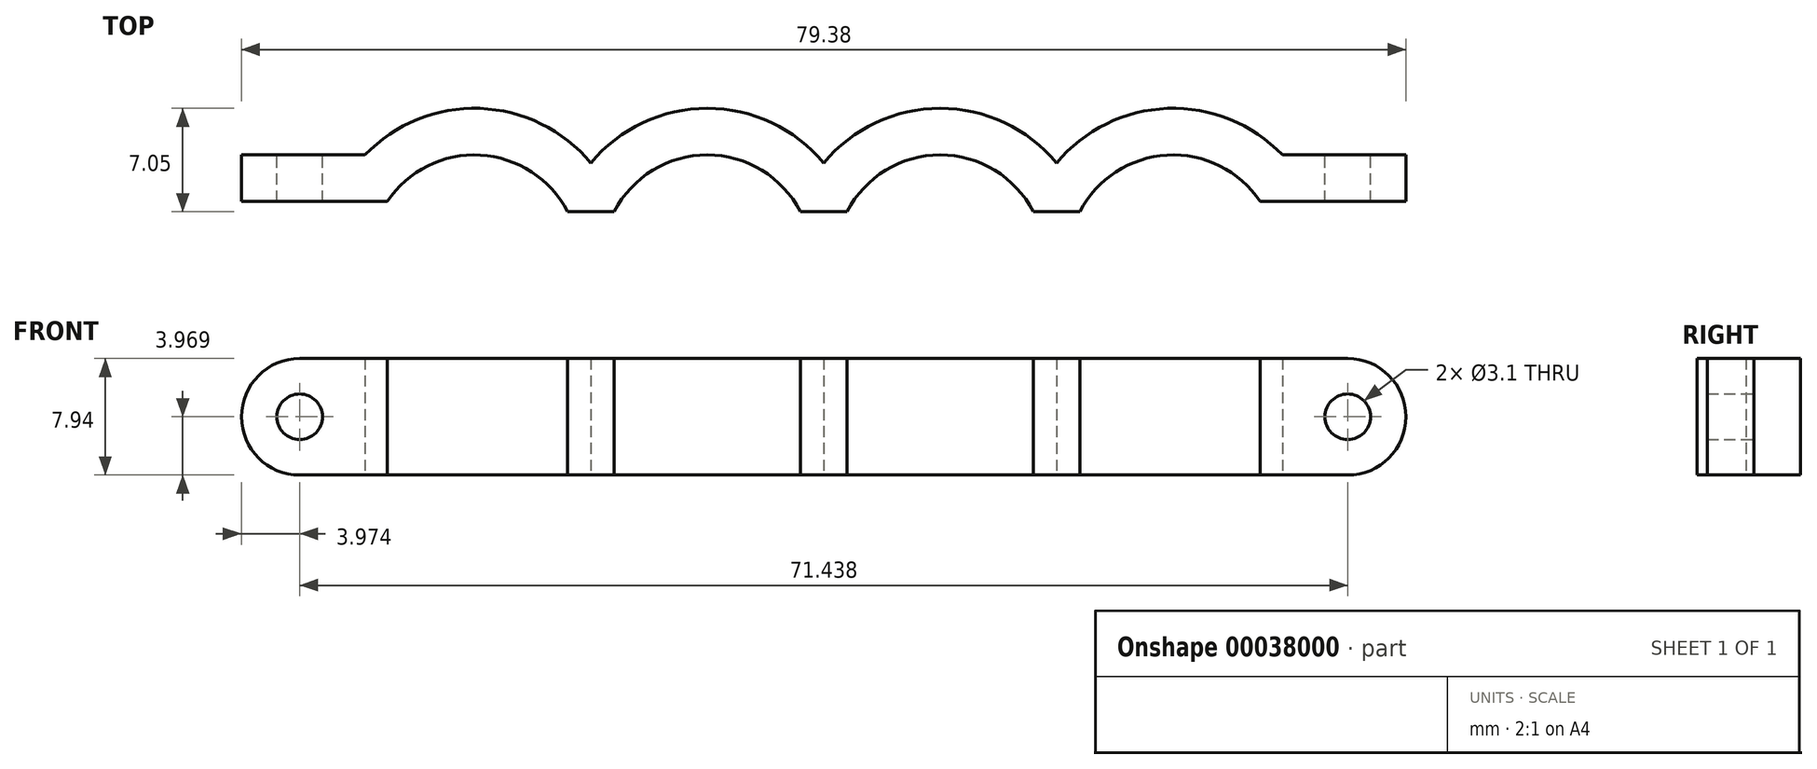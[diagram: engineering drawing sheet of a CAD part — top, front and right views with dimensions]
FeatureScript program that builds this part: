
annotation { "Feature Type Name" : "Feature", "Feature Type Description" : "" }
export const myFeature = defineFeature(function(context is Context, id is Id, definition is map)
    precondition{}
    {
        {
            var Q0;
            Q0=qCreatedBy(makeId("Top.planeOp"),FACE);
            var sketch = newSketch(context, id + "F0", { "sketchPlane" : qUnion([Q0])});
            skLineSegment(sketch, "E0.bottom", {"start": v(0, 0) * mm, "end": v(-9.94, 0) * mm});
            skLineSegment(sketch, "E0.right", {"start": v(-9.94, 0) * mm, "end": v(-9.94, 3.18) * mm});
            skArc(sketch, "E1", {"start": v(12.29, -0.7) * mm, "mid": v(6.34, 3.16) * mm, "end": v(0, 0) * mm});
            skLineSegment(sketch, "E2", {"start": v(0, 0) * mm, "end": v(5.94, 0) * mm, "construction": true});
            skLineSegment(sketch, "E3", {"start": v(5.94, 0) * mm, "end": v(21.81, 0) * mm, "construction": true});
            skLineSegment(sketch, "E4", {"start": v(13.88, -0.7) * mm, "end": v(13.88, 0) * mm, "construction": true});
            skLineSegment(sketch, "E5", {"start": v(21.81, 0) * mm, "end": v(37.69, 0) * mm, "construction": true});
            skLineSegment(sketch, "E6", {"start": v(37.69, 0) * mm, "end": v(53.56, 0) * mm, "construction": true});
            skLineSegment(sketch, "E7", {"start": v(29.75, -0.7) * mm, "end": v(29.75, 0) * mm, "construction": true});
            skLineSegment(sketch, "E8", {"start": v(45.63, -0.7) * mm, "end": v(45.63, 0) * mm, "construction": true});
            skLineSegment(sketch, "E9", {"start": v(12.29, -0.7) * mm, "end": v(15.46, -0.7) * mm});
            skLineSegment(sketch, "E10", {"start": v(28.16, -0.7) * mm, "end": v(31.34, -0.7) * mm});
            skLineSegment(sketch, "E11", {"start": v(44.04, -0.7) * mm, "end": v(47.21, -0.7) * mm});
            skArc(sketch, "E12", {"start": v(28.16, -0.7) * mm, "mid": v(21.81, 3.18) * mm, "end": v(15.46, -0.7) * mm});
            skArc(sketch, "E13", {"start": v(44.04, -0.7) * mm, "mid": v(37.69, 3.18) * mm, "end": v(31.34, -0.7) * mm});
            skArc(sketch, "E14", {"start": v(59.5, 0) * mm, "mid": v(53.16, 3.16) * mm, "end": v(47.21, -0.7) * mm});
            skLineSegment(sketch, "E15", {"start": v(53.56, 0) * mm, "end": v(59.5, 0) * mm, "construction": true});
            skArc(sketch, "E16", {"start": v(61.01, 3.18) * mm, "mid": v(53.2, 6.34) * mm, "end": v(45.63, 2.62) * mm});
            skArc(sketch, "E17", {"start": v(45.63, 2.62) * mm, "mid": v(37.69, 6.35) * mm, "end": v(29.75, 2.62) * mm});
            skArc(sketch, "E18", {"start": v(13.88, 2.62) * mm, "mid": v(6.3, 6.34) * mm, "end": v(-1.5, 3.17) * mm});
            skArc(sketch, "E19", {"start": v(29.75, 2.62) * mm, "mid": v(21.81, 6.35) * mm, "end": v(13.88, 2.62) * mm});
            skLineSegment(sketch, "E20", {"start": v(-9.94, 3.18) * mm, "end": v(-1.5, 3.18) * mm});
            skLineSegment(sketch, "E21", {"start": v(59.5, 0) * mm, "end": v(69.44, 0) * mm});
            skLineSegment(sketch, "E22", {"start": v(69.44, 0) * mm, "end": v(69.44, 3.18) * mm});
            skLineSegment(sketch, "E23", {"start": v(69.44, 3.17) * mm, "end": v(61.01, 3.17) * mm});
            skLineSegment(sketch, "E24", {"start": v(21.81, 3.18) * mm, "end": v(21.81, 6.35) * mm, "construction": true});
            skLineSegment(sketch, "E25", {"start": v(21.81, 0) * mm, "end": v(21.81, -3.97) * mm, "construction": true});
            skLineSegment(sketch, "E26", {"start": v(5.94, 0) * mm, "end": v(5.94, -3.97) * mm, "construction": true});
            skLineSegment(sketch, "E27", {"start": v(53.56, 0) * mm, "end": v(53.56, -3.97) * mm, "construction": true});
            skLineSegment(sketch, "E28", {"start": v(37.69, 0) * mm, "end": v(37.69, -3.97) * mm, "construction": true});
            skSolve(sketch);
        }
        {
            var Q0;
            Q0 = qSketchRegion(id + "F0", true);
            extrude(context, id + "F1", {"entities" : qUnion([Q0]), "depth" : 7.94 * mm});
        }
        {
            var Q0;
            Q0=makeQuery(id+"F1.opExtrude","SWEPT_FACE",FACE,{"disambiguationData":[OSD([sQuery(id+"F0.wireOp",EDGE,"E20")])]});
            var sketch = newSketch(context, id + "F2", { "sketchPlane" : qUnion([Q0])});
            skLineSegment(sketch, "E29", {"start": v(9.94, 3.97) * mm, "end": v(5.97, 3.97) * mm, "construction": true});
            skLineSegment(sketch, "E30", {"start": v(-69.44, 3.97) * mm, "end": v(-65.47, 3.97) * mm, "construction": true});
            skCircle(sketch, "E31", {"center": v(5.97, 3.97) * mm, "radius": 1.55 * mm});
            skCircle(sketch, "E32", {"center": v(-65.47, 3.97) * mm, "radius": 1.55 * mm});
            skSolve(sketch);
        }
        {
            var Q0;
            Q0 = qSketchRegion(id + "F2", true);
            var Q1;
            Q1=makeQuery(id+"F1.opExtrude","SWEPT_FACE",FACE,{"disambiguationData":[OSD([sQuery(id+"F0.wireOp",EDGE,"E0.bottom")])]});
            extrude(context, id + "F3", {"entities" : qUnion([Q0]), "operationType" : NewBodyOperationType.REMOVE, "endBound" : BoundingType.UP_TO_SURFACE, "oppositeDirection" : true, "endBoundEntityFace" : qUnion([Q1]), "depth" : 25.4 * mm});
        }
        {
            var Q0;
            Q0=makeQuery(id+"F1.opExtrude","SWEPT_FACE",FACE,{"disambiguationData":[OSD([sQuery(id+"F0.wireOp",EDGE,"E20")])]});
            var sketch = newSketch(context, id + "F4", { "sketchPlane" : qUnion([Q0])});
            skCircle(sketch, "E33", {"center": v(5.97, 3.97) * mm, "radius": 3.18 * mm});
            skCircle(sketch, "E34", {"center": v(-65.47, 3.97) * mm, "radius": 3.18 * mm});
            skSolve(sketch);
        }
        {
            var Q0;
            Q0 = qSketchRegion(id + "F4", true);
            var Q1;
            Q1=makeQuery(id+"F1.opExtrude","SWEPT_FACE",FACE,{"disambiguationData":[OSD([sQuery(id+"F0.wireOp",EDGE,"E16")])]});
            extrude(context, id + "F5", {"entities" : qUnion([Q0]), "operationType" : NewBodyOperationType.REMOVE, "endBoundEntityFace" : qUnion([Q1]), "depth" : 25.4 * mm});
        }
        {
            var Q0;
            Q0=makeQuery(id+"F1.opExtrude","CAP_EDGE",EDGE,{"disambiguationData":[OSD([sQuery(id+"F0.wireOp",EDGE,"E22")])],"isStart":false});
            var Q1;
            Q1=makeQuery(id+"F1.opExtrude","CAP_EDGE",EDGE,{"disambiguationData":[OSD([sQuery(id+"F0.wireOp",EDGE,"E22")])],"isStart":true});
            var Q2;
            Q2=makeQuery(id+"F1.opExtrude","CAP_EDGE",EDGE,{"disambiguationData":[OSD([sQuery(id+"F0.wireOp",EDGE,"E0.right")])],"isStart":false});
            var Q3;
            Q3=makeQuery(id+"F1.opExtrude","CAP_EDGE",EDGE,{"disambiguationData":[OSD([sQuery(id+"F0.wireOp",EDGE,"E0.right")])],"isStart":true});
            fillet(context, id + "F6", {"entities" : qUnion([Q0, Q1, Q2, Q3]), "radius" : 3.97 * mm, "tangentPropagation" : true, "allowEdgeOverflow" : false});
        }
    });
